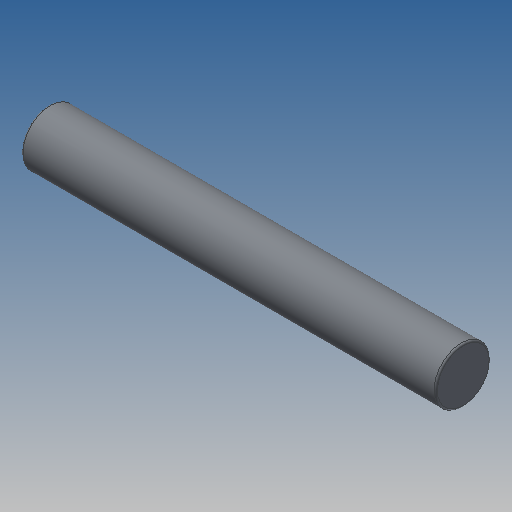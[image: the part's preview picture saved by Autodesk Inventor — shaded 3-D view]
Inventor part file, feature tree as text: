
AUTODESK INVENTOR PART (.ipt)
format: ipt  version: 2022.2 (Build 262287010, 287A)  size: 129,536 bytes
history: native  units: mm (DEFAULTED — no unit token found)
features: extrude x1, fillet x1, sketch x1
ambient origin geometry x8: Origin, YZ Plane, XZ Plane, XY Plane, X Axis, Y Axis, Z Axis, Center Point
bodies: Solid2 (feature_tree)
feature tree (3):
  extrude  "Extrusion7"  Depth=24.0mm TaperAngle=0.0deg
  fillet  "Fillet2"  Radius=0.1mm
  sketch  "Sketch1"  dims[d26=3.2mm d27=24.0mm d28=0.0mm d29=0.1mm d30=0.0mm d31=0.0mm]
